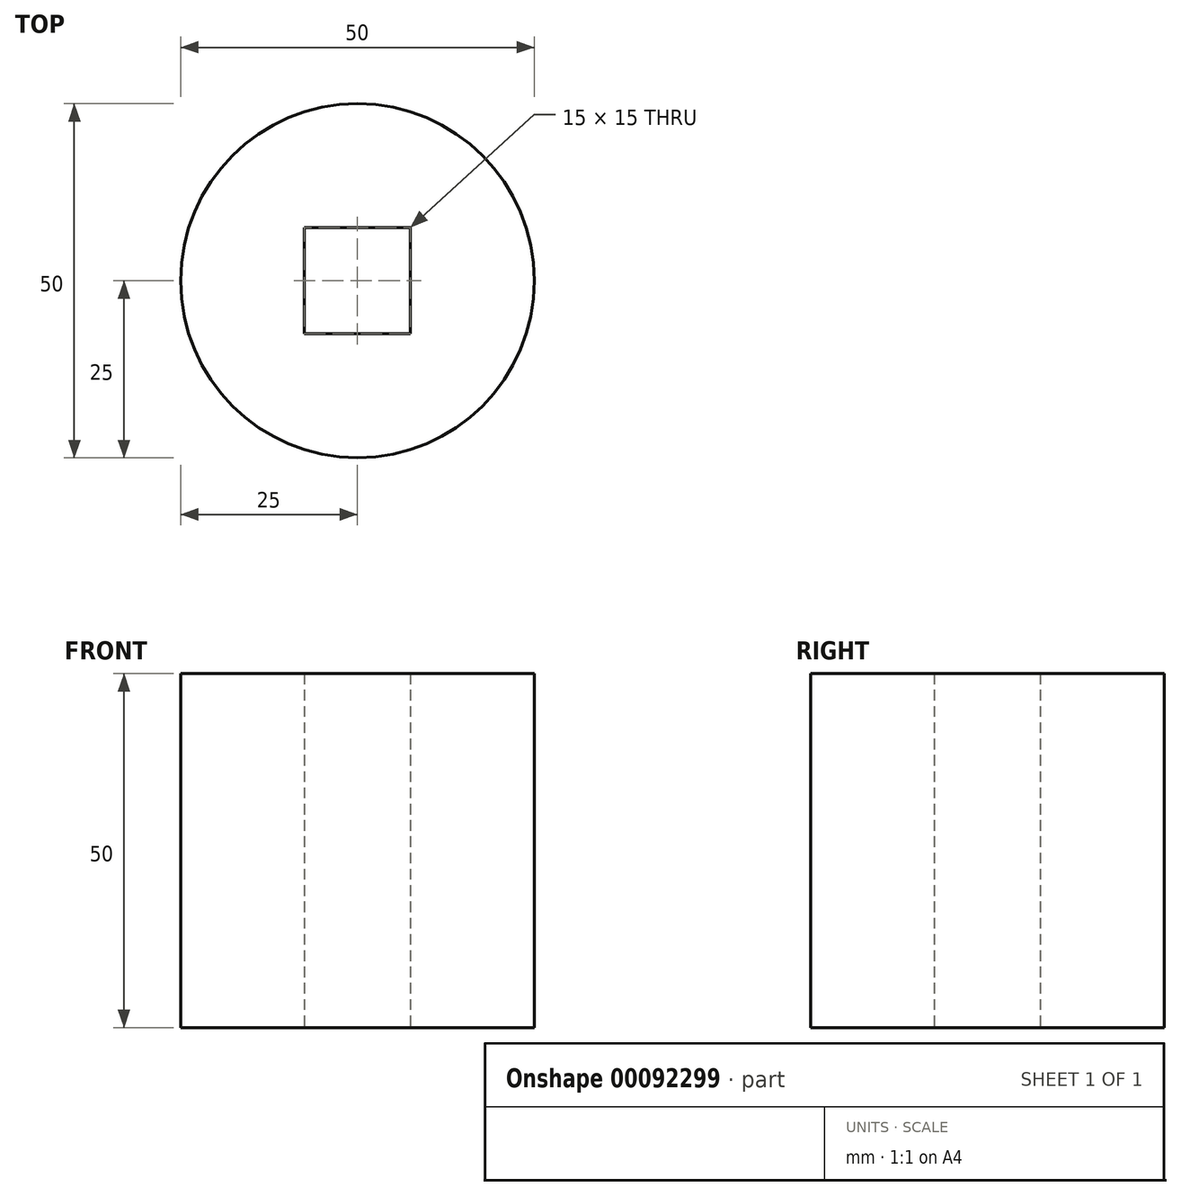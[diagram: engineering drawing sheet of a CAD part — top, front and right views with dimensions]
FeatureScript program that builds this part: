
annotation { "Feature Type Name" : "Feature", "Feature Type Description" : "" }
export const myFeature = defineFeature(function(context is Context, id is Id, definition is map)
    precondition{}
    {
        {
            var Q0;
            Q0=qCreatedBy(makeId("Top.planeOp"),FACE);
            var sketch = newSketch(context, id + "F0", { "sketchPlane" : qUnion([Q0])});
            skCircle(sketch, "E0", {"center": v(0, 0) * mm, "radius": 25 * mm});
            skLineSegment(sketch, "E1.bottom", {"start": v(7.5, 7.5) * mm, "end": v(-7.5, 7.5) * mm});
            skLineSegment(sketch, "E1.top", {"start": v(7.5, -7.5) * mm, "end": v(-7.5, -7.5) * mm});
            skLineSegment(sketch, "E1.left", {"start": v(7.5, 7.5) * mm, "end": v(7.5, -7.5) * mm});
            skLineSegment(sketch, "E1.right", {"start": v(-7.5, 7.5) * mm, "end": v(-7.5, -7.5) * mm});
            skSolve(sketch);
        }
        {
            var Q0;
            Q0=makeQuery(id+"F0.imprint","IMPRINT",FACE,{"disambiguationData":[TD([[makeQuery(id+"F0.imprint","IMPRINT",EDGE,{"derivedFrom":sQuery(id+"F0.wireOp",EDGE,"E0")}),1.0]])]});
            extrude(context, id + "F1", {"entities" : qUnion([Q0]), "depth" : 50 * mm});
        }
    });
